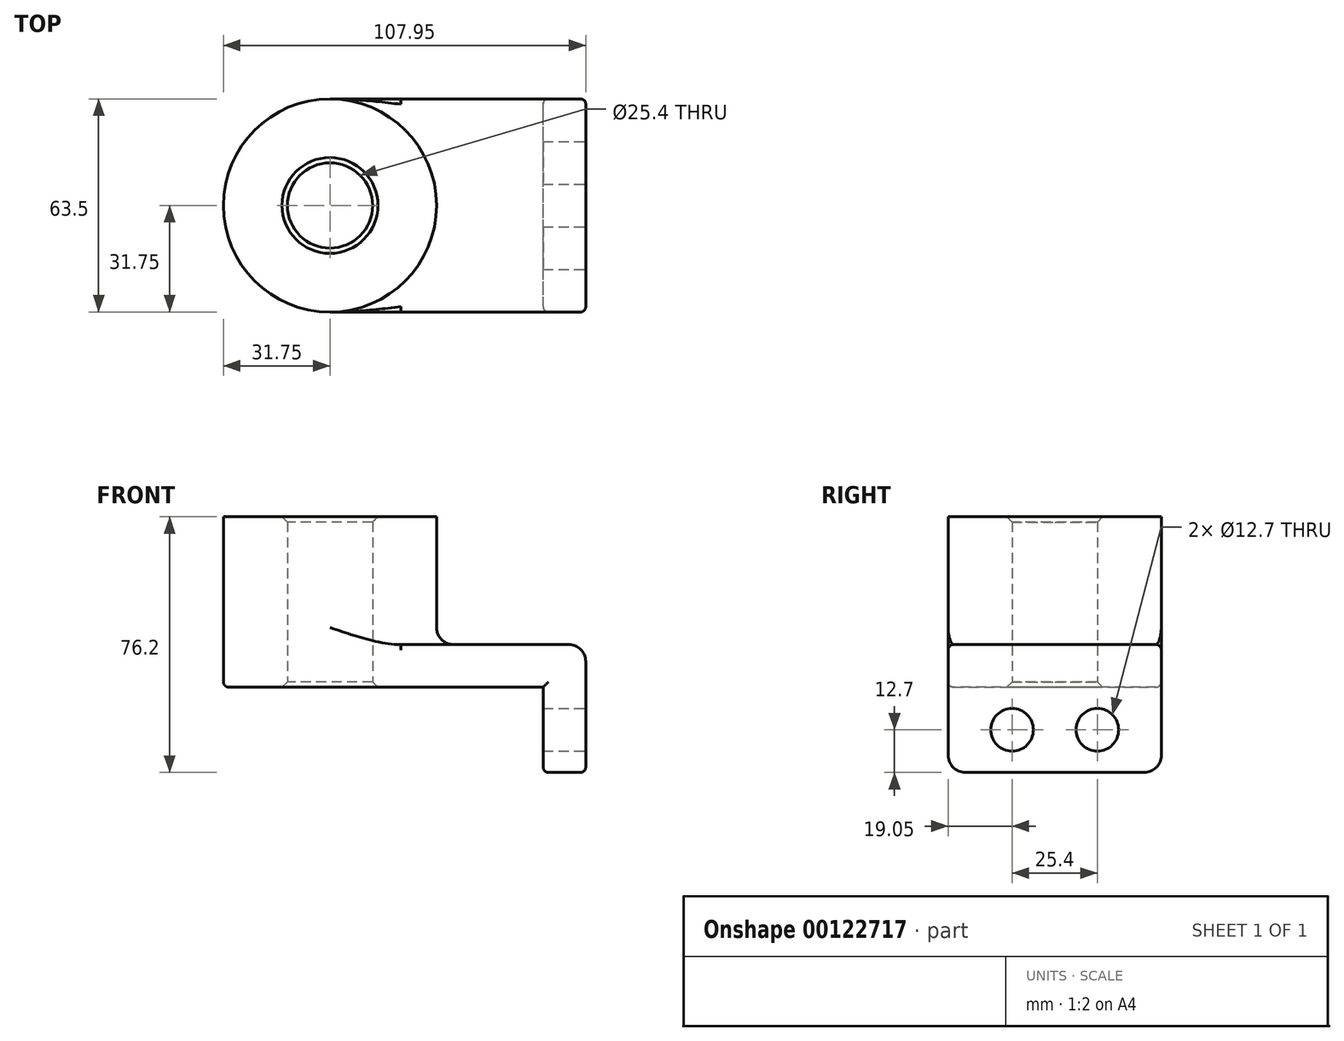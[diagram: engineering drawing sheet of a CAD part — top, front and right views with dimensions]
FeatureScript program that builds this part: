
annotation { "Feature Type Name" : "Feature", "Feature Type Description" : "" }
export const myFeature = defineFeature(function(context is Context, id is Id, definition is map)
    precondition{}
    {
        {
            var Q0;
            Q0=qCreatedBy(makeId("Top.planeOp"),FACE);
            var sketch = newSketch(context, id + "F0", { "sketchPlane" : qUnion([Q0])});
            skLineSegment(sketch, "E0.bottom", {"start": v(38.1, -31.75) * mm, "end": v(-38.1, -31.75) * mm});
            skLineSegment(sketch, "E0.top", {"start": v(38.1, 31.75) * mm, "end": v(-38.1, 31.75) * mm});
            skLineSegment(sketch, "E0.left", {"start": v(38.1, -31.75) * mm, "end": v(38.1, 31.75) * mm});
            skLineSegment(sketch, "E0.right", {"start": v(-38.1, -31.75) * mm, "end": v(-38.1, 31.75) * mm});
            skPoint(sketch, "E0.middle", {"position": v(0, 0) * mm});
            skCircle(sketch, "E1", {"center": v(-38.1, 0) * mm, "radius": 31.75 * mm});
            skCircle(sketch, "E2", {"center": v(-38.1, 0) * mm, "radius": 12.7 * mm});
            skSolve(sketch);
        }
        {
            var Q0;
            Q0 = qSketchRegion(id + "F0", true);
            extrude(context, id + "F1", {"entities" : qUnion([Q0]), "depth" : 12.7 * mm});
        }
        {
            var Q0;
            {var subQ1=sQuery(id+"F0.wireOp",EDGE,"E0.right");var subQ3=sQuery(id+"F0.wireOp",EDGE,"E2");var subQ4=makeQuery(id+"F0.imprint","INTERSECT",VERTEX,{"disambiguationData":[OD(0.0)],"derivedFrom":[subQ1,subQ3]});Q0=makeQuery(id+"F0.imprint","IMPRINT",FACE,{"disambiguationData":[TD([[makeQuery(id+"F0.imprint","IMPRINT",EDGE,{"disambiguationData":[TD([[subQ4,1.0]])],"derivedFrom":subQ3}),-1.0]])]});}
            var Q1;
            {var subQ1=sQuery(id+"F0.wireOp",EDGE,"E0.right");var subQ3=sQuery(id+"F0.wireOp",EDGE,"E2");var subQ4=makeQuery(id+"F0.imprint","INTERSECT",VERTEX,{"disambiguationData":[OD(0.0)],"derivedFrom":[subQ1,subQ3]});Q1=makeQuery(id+"F0.imprint","IMPRINT",FACE,{"disambiguationData":[TD([[makeQuery(id+"F0.imprint","IMPRINT",EDGE,{"disambiguationData":[TD([[subQ4,-1.0]])],"derivedFrom":subQ3}),-1.0]])]});}
            extrude(context, id + "F2", {"entities" : qUnion([Q0, Q1]), "operationType" : NewBodyOperationType.ADD, "depth" : 50.8 * mm});
        }
        {
            var Q0;
            Q0=makeQuery(id+"F1.opExtrude","SWEPT_FACE",FACE,{"disambiguationData":[OSD([sQuery(id+"F0.wireOp",EDGE,"E0.left")])]});
            var sketch = newSketch(context, id + "F3", { "sketchPlane" : qUnion([Q0])});
            skLineSegment(sketch, "E3.bottom", {"start": v(-31.75, 12.7) * mm, "end": v(31.75, 12.7) * mm});
            skLineSegment(sketch, "E3.top", {"start": v(-31.75, -25.4) * mm, "end": v(31.75, -25.4) * mm});
            skLineSegment(sketch, "E3.left", {"start": v(-31.75, 12.7) * mm, "end": v(-31.75, -25.4) * mm});
            skLineSegment(sketch, "E3.right", {"start": v(31.75, 12.7) * mm, "end": v(31.75, -25.4) * mm});
            skCircle(sketch, "E4", {"center": v(-12.7, -12.7) * mm, "radius": 6.35 * mm});
            skLineSegment(sketch, "E5", {"start": v(0, -25.4) * mm, "end": v(0, 0) * mm, "construction": true});
            skCircle(sketch, "E6.MirrorC", {"center": v(12.7, -12.7) * mm, "radius": 6.35 * mm});
            skSolve(sketch);
        }
        {
            var Q0;
            Q0 = qSketchRegion(id + "F3", true);
            extrude(context, id + "F4", {"entities" : qUnion([Q0]), "operationType" : NewBodyOperationType.ADD, "oppositeDirection" : true, "depth" : 12.7 * mm});
        }
        {
            var Q0;
            {var subQ0=sQuery(id+"F0.wireOp",EDGE,"E1");Q0=makeQuery(id+"F2.boolean.opBoolean","INTERSECT",EDGE,{"derivedFrom":[makeQuery(id+"F1.opExtrude","CAP_FACE",FACE,{"disambiguationData":[OSD([sQuery(id+"F0.wireOp",EDGE,"E0.bottom"),sQuery(id+"F0.wireOp",EDGE,"E0.top"),sQuery(id+"F0.wireOp",EDGE,"E0.left"),subQ0,sQuery(id+"F0.wireOp",EDGE,"E2")])],"isStart":false}),makeQuery(id+"F2.opExtrude","SWEPT_FACE",FACE,{"disambiguationData":[OSD([subQ0])]})]});}
            var Q1;
            Q1=makeQuery(id+"F1.opExtrude","CAP_EDGE",EDGE,{"disambiguationData":[OSD([sQuery(id+"F0.wireOp",EDGE,"E0.left")])],"isStart":false});
            var Q2;
            Q2=makeQuery(id+"F4.opExtrude","SWEPT_EDGE",EDGE,{"disambiguationData":[OSD([sQuery(id+"F3.wireOp",EDGE,"E3.top"),sQuery(id+"F3.wireOp",EDGE,"E3.left")])]});
            var Q3;
            Q3=makeQuery(id+"F4.opExtrude","SWEPT_EDGE",EDGE,{"disambiguationData":[OSD([sQuery(id+"F3.wireOp",EDGE,"E3.top"),sQuery(id+"F3.wireOp",EDGE,"E3.right")])]});
            fillet(context, id + "F5", {"entities" : qUnion([Q0, Q1, Q2, Q3]), "radius" : 5.08 * mm, "tangentPropagation" : true, "allowEdgeOverflow" : false});
        }
        {
            var Q0;
            Q0=makeQuery(id+"F1.opExtrude","CAP_EDGE",EDGE,{"disambiguationData":[OSD([sQuery(id+"F0.wireOp",EDGE,"E0.bottom")])],"isStart":false});
            var Q1;
            Q1=makeQuery(id+"F1.opExtrude","CAP_EDGE",EDGE,{"disambiguationData":[OSD([sQuery(id+"F0.wireOp",EDGE,"E0.bottom")])],"isStart":true});
            var Q2;
            Q2=makeQuery(id+"F4.opExtrude","CAP_EDGE",EDGE,{"disambiguationData":[OSD([sQuery(id+"F3.wireOp",EDGE,"E3.left")])],"isStart":false});
            fillet(context, id + "F6", {"entities" : qUnion([Q0, Q1, Q2]), "radius" : 1.59 * mm, "tangentPropagation" : true, "allowEdgeOverflow" : false});
        }
        {
            var Q0;
            Q0=makeQuery(id+"F2.opExtrude","CAP_EDGE",EDGE,{"disambiguationData":[OSD([sQuery(id+"F0.wireOp",EDGE,"E2")])],"isStart":false});
            var Q1;
            Q1=makeQuery(id+"F1.opExtrude","CAP_EDGE",EDGE,{"disambiguationData":[OSD([sQuery(id+"F0.wireOp",EDGE,"E2")])],"isStart":true});
            chamfer(context, id + "F7", {"entities" : qUnion([Q0, Q1]), "width" : 1.59 * mm, "tangentPropagation" : true});
        }
    });
